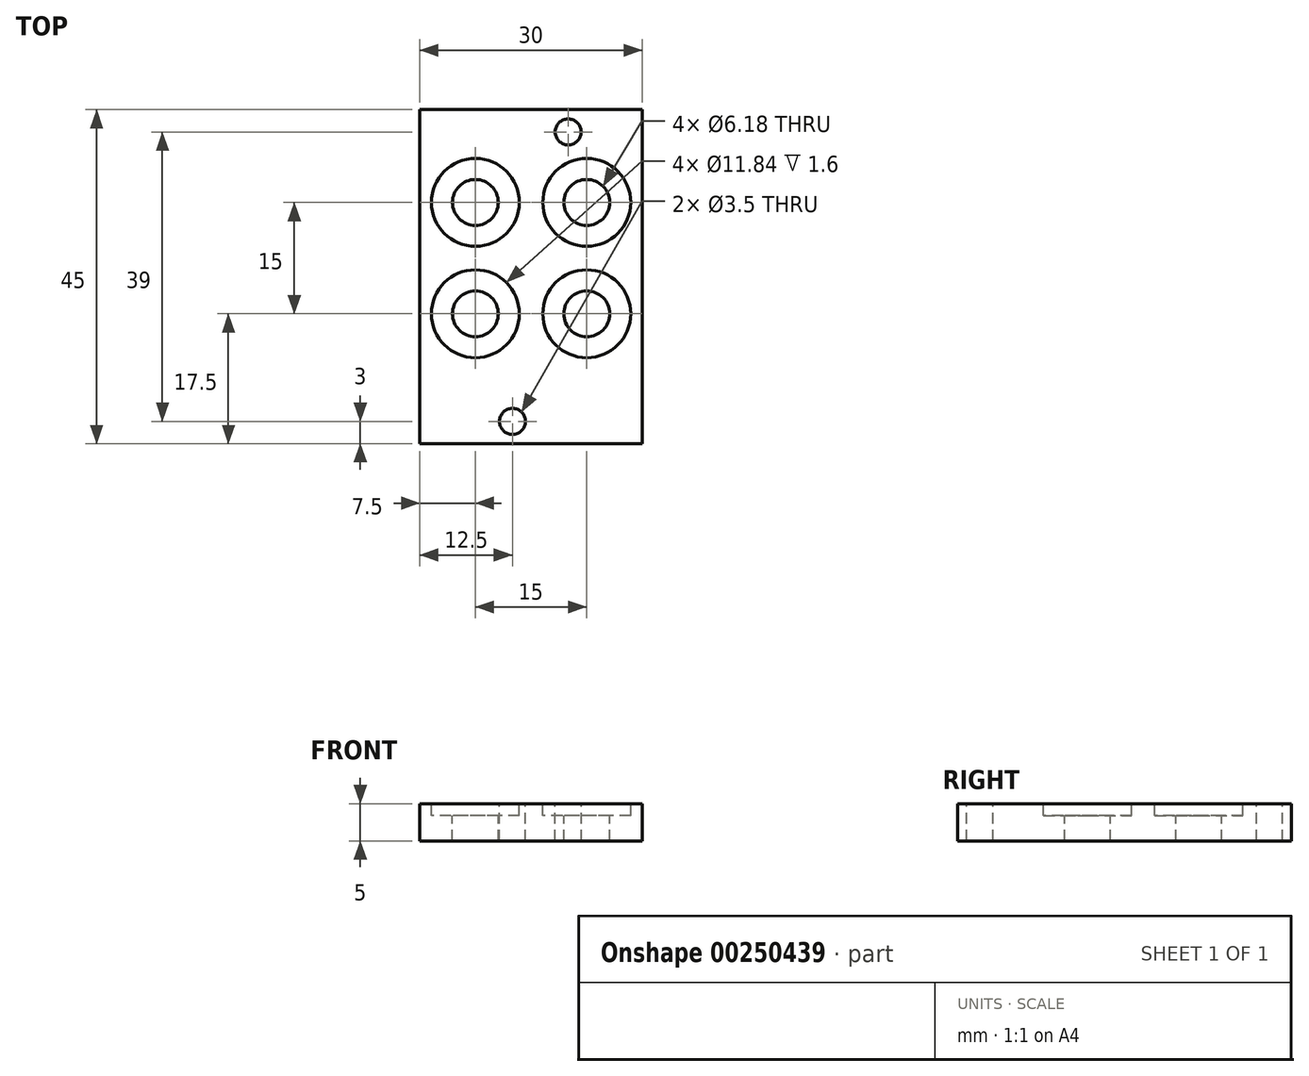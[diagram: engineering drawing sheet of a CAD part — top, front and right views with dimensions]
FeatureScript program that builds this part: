
annotation { "Feature Type Name" : "Feature", "Feature Type Description" : "" }
export const myFeature = defineFeature(function(context is Context, id is Id, definition is map)
    precondition{}
    {
        {
            var Q0;
            Q0=qCreatedBy(makeId("Top.planeOp"),FACE);
            var sketch = newSketch(context, id + "F0", { "sketchPlane" : qUnion([Q0])});
            skLineSegment(sketch, "E0.bottom", {"start": v(-15, 22.5) * mm, "end": v(15, 22.5) * mm});
            skLineSegment(sketch, "E0.top", {"start": v(-15, -22.5) * mm, "end": v(15, -22.5) * mm});
            skLineSegment(sketch, "E0.left", {"start": v(-15, 22.5) * mm, "end": v(-15, -22.5) * mm});
            skLineSegment(sketch, "E0.right", {"start": v(15, 22.5) * mm, "end": v(15, -22.5) * mm});
            skSolve(sketch);
        }
        {
            var Q0;
            Q0 = qSketchRegion(id + "F0", true);
            extrude(context, id + "F1", {"entities" : qUnion([Q0]), "depth" : 5 * mm});
        }
        {
            var Q0;
            Q0=makeQuery(id+"F1.opExtrude","CAP_FACE",FACE,{"disambiguationData":[OSD([sQuery(id+"F0.wireOp",EDGE,"E0.bottom"),sQuery(id+"F0.wireOp",EDGE,"E0.top"),sQuery(id+"F0.wireOp",EDGE,"E0.left"),sQuery(id+"F0.wireOp",EDGE,"E0.right")])],"isStart":false});
            var sketch = newSketch(context, id + "F2", { "sketchPlane" : qUnion([Q0])});
            skCircle(sketch, "E1", {"center": v(-7.5, 10) * mm, "radius": 3.09 * mm});
            skCircle(sketch, "E2", {"center": v(-7.5, -5) * mm, "radius": 3.09 * mm});
            skCircle(sketch, "E3", {"center": v(7.5, 10) * mm, "radius": 3.09 * mm});
            skCircle(sketch, "E4", {"center": v(7.5, -5) * mm, "radius": 3.09 * mm});
            skSolve(sketch);
        }
        {
            var Q0;
            Q0 = qSketchRegion(id + "F2", true);
            extrude(context, id + "F3", {"entities" : qUnion([Q0]), "operationType" : NewBodyOperationType.REMOVE, "endBound" : BoundingType.UP_TO_NEXT, "oppositeDirection" : true, "depth" : 25 * mm});
        }
        {
            var Q0;
            Q0=makeQuery(id+"F1.opExtrude","CAP_FACE",FACE,{"disambiguationData":[OSD([sQuery(id+"F0.wireOp",EDGE,"E0.bottom"),sQuery(id+"F0.wireOp",EDGE,"E0.top"),sQuery(id+"F0.wireOp",EDGE,"E0.left"),sQuery(id+"F0.wireOp",EDGE,"E0.right")])],"isStart":false});
            var sketch = newSketch(context, id + "F4", { "sketchPlane" : qUnion([Q0])});
            skCircle(sketch, "E5", {"center": v(-7.5, 10) * mm, "radius": 5.92 * mm});
            skCircle(sketch, "E6", {"center": v(7.5, 10) * mm, "radius": 5.92 * mm});
            skCircle(sketch, "E7", {"center": v(7.5, -5) * mm, "radius": 5.92 * mm});
            skCircle(sketch, "E8", {"center": v(-7.5, -5) * mm, "radius": 5.92 * mm});
            skSolve(sketch);
        }
        {
            var Q0;
            Q0 = qSketchRegion(id + "F4", true);
            extrude(context, id + "F5", {"entities" : qUnion([Q0]), "operationType" : NewBodyOperationType.REMOVE, "oppositeDirection" : true, "depth" : 1.6 * mm});
        }
        {
            var Q0;
            Q0=makeQuery(id+"F1.opExtrude","CAP_FACE",FACE,{"disambiguationData":[OSD([sQuery(id+"F0.wireOp",EDGE,"E0.bottom"),sQuery(id+"F0.wireOp",EDGE,"E0.top"),sQuery(id+"F0.wireOp",EDGE,"E0.left"),sQuery(id+"F0.wireOp",EDGE,"E0.right")])],"isStart":false});
            var sketch = newSketch(context, id + "F6", { "sketchPlane" : qUnion([Q0])});
            skCircle(sketch, "E9", {"center": v(5, 19.5) * mm, "radius": 1.75 * mm});
            skCircle(sketch, "E10", {"center": v(-2.5, -19.5) * mm, "radius": 1.75 * mm});
            skSolve(sketch);
        }
        {
            var Q0;
            Q0 = qSketchRegion(id + "F6", true);
            extrude(context, id + "F7", {"entities" : qUnion([Q0]), "operationType" : NewBodyOperationType.REMOVE, "endBound" : BoundingType.UP_TO_NEXT, "oppositeDirection" : true, "depth" : 25 * mm});
        }
    });
